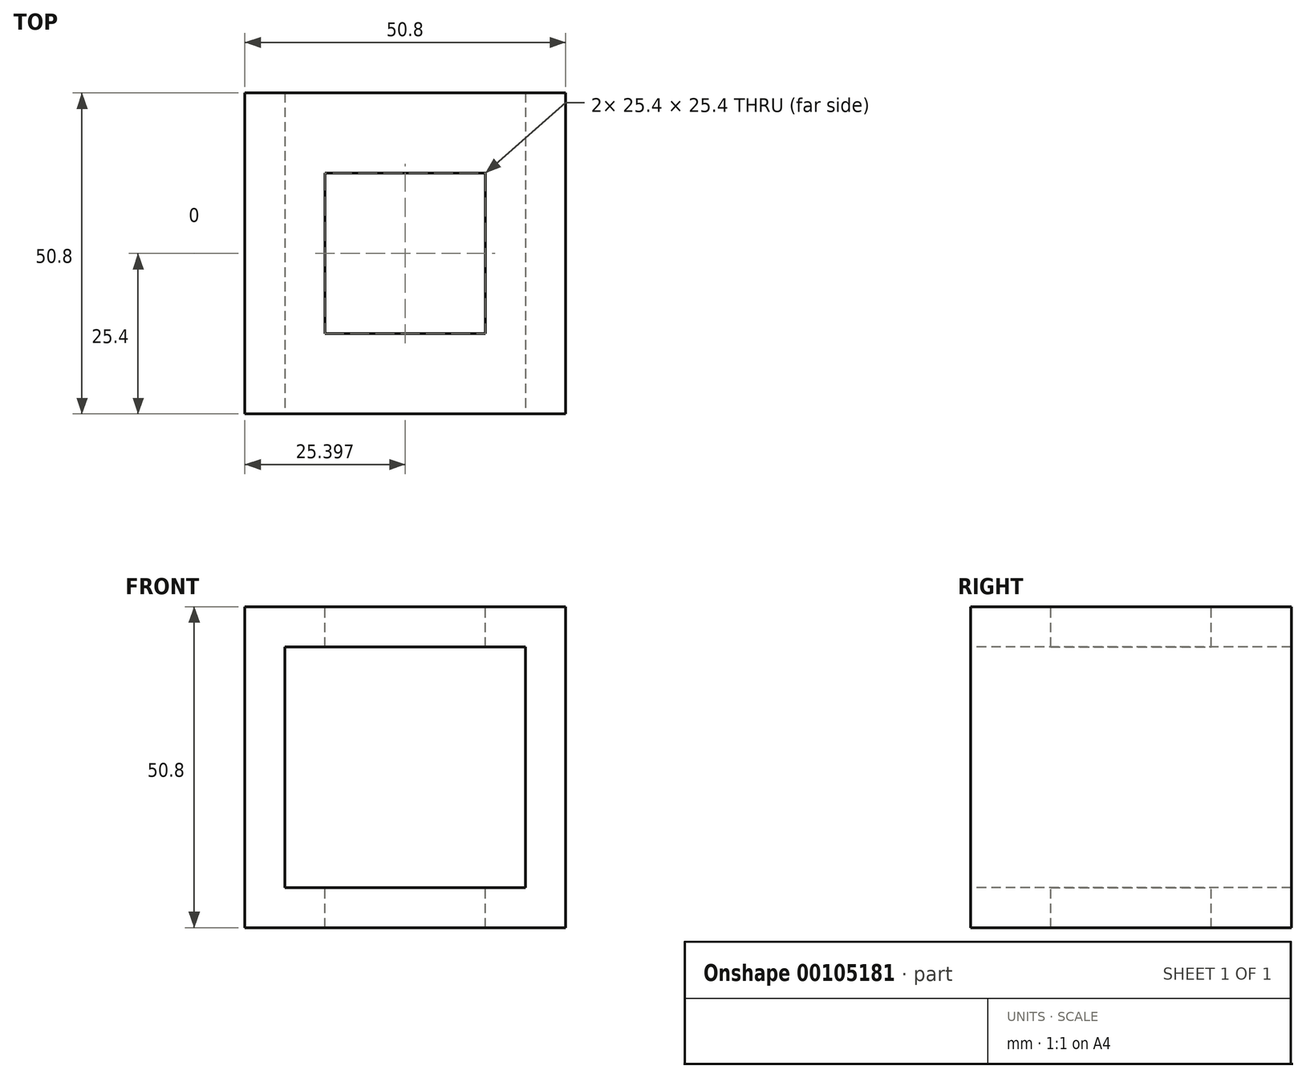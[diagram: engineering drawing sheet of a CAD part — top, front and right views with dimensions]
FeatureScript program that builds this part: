
annotation { "Feature Type Name" : "Feature", "Feature Type Description" : "" }
export const myFeature = defineFeature(function(context is Context, id is Id, definition is map)
    precondition{}
    {
        {
            var Q0;
            Q0=qCreatedBy(makeId("Front.planeOp"),FACE);
            var sketch = newSketch(context, id + "F0", { "sketchPlane" : qUnion([Q0])});
            skLineSegment(sketch, "E0", {"start": v(-98.96, 44.89) * mm, "end": v(-98.96, -5.91) * mm});
            skLineSegment(sketch, "E1", {"start": v(-98.96, -5.91) * mm, "end": v(-48.16, -5.91) * mm});
            skLineSegment(sketch, "E2", {"start": v(-48.16, -5.91) * mm, "end": v(-48.16, 44.89) * mm});
            skLineSegment(sketch, "E3", {"start": v(-48.16, 44.89) * mm, "end": v(-98.96, 44.89) * mm});
            skSolve(sketch);
        }
        {
            var Q0;
            Q0 = qSketchRegion(id + "F0", true);
            extrude(context, id + "F1", {"entities" : qUnion([Q0]), "depth" : 50.8 * mm});
        }
        {
            var Q0;
            Q0=makeQuery(id+"F1.opExtrude","CAP_FACE",FACE,{"disambiguationData":[OSD([sQuery(id+"F0.wireOp",EDGE,"E0"),sQuery(id+"F0.wireOp",EDGE,"E1"),sQuery(id+"F0.wireOp",EDGE,"E2"),sQuery(id+"F0.wireOp",EDGE,"E3")])],"isStart":false});
            var sketch = newSketch(context, id + "F2", { "sketchPlane" : qUnion([Q0])});
            skLineSegment(sketch, "E4.bottom", {"start": v(-92.61, 38.54) * mm, "end": v(-54.51, 38.54) * mm});
            skLineSegment(sketch, "E4.top", {"start": v(-92.61, 0.44) * mm, "end": v(-54.51, 0.44) * mm});
            skLineSegment(sketch, "E4.left", {"start": v(-92.61, 38.54) * mm, "end": v(-92.61, 0.44) * mm});
            skLineSegment(sketch, "E4.right", {"start": v(-54.51, 38.54) * mm, "end": v(-54.51, 0.44) * mm});
            skLineSegment(sketch, "E5", {"start": v(-98.96, 44.89) * mm, "end": v(-48.16, -5.91) * mm, "construction": true});
            skSolve(sketch);
        }
        {
            var Q0;
            Q0=makeQuery(id+"F2.imprint","IMPRINT",FACE,{"disambiguationData":[TD([[makeQuery(id+"F2.imprint","IMPRINT",EDGE,{"derivedFrom":sQuery(id+"F2.wireOp",EDGE,"E4.bottom")}),-1.0]])]});
            extrude(context, id + "F3", {"entities" : qUnion([Q0]), "operationType" : NewBodyOperationType.REMOVE, "endBound" : BoundingType.THROUGH_ALL, "oppositeDirection" : true, "depth" : 25.4 * mm});
        }
        {
            var Q0;
            Q0=makeQuery(id+"F1.opExtrude","SWEPT_FACE",FACE,{"disambiguationData":[OSD([sQuery(id+"F0.wireOp",EDGE,"E3")])]});
            var sketch = newSketch(context, id + "F4", { "sketchPlane" : qUnion([Q0])});
            skLineSegment(sketch, "E6.bottom", {"start": v(-86.26, -12.7) * mm, "end": v(-60.86, -12.7) * mm});
            skLineSegment(sketch, "E6.top", {"start": v(-86.26, -38.1) * mm, "end": v(-60.86, -38.1) * mm});
            skLineSegment(sketch, "E6.left", {"start": v(-86.26, -12.7) * mm, "end": v(-86.26, -38.1) * mm});
            skLineSegment(sketch, "E6.right", {"start": v(-60.86, -12.7) * mm, "end": v(-60.86, -38.1) * mm});
            skSolve(sketch);
        }
        {
            var Q0;
            Q0=makeQuery(id+"F4.imprint","IMPRINT",FACE,{"disambiguationData":[TD([[makeQuery(id+"F4.imprint","IMPRINT",EDGE,{"derivedFrom":sQuery(id+"F4.wireOp",EDGE,"E6.bottom")}),-1.0]])]});
            var Q1;
            Q1=sQuery(id+"F4.wireOp",EDGE,"E6.bottom");
            var Q2;
            Q2=sQuery(id+"F4.wireOp",EDGE,"E6.left");
            var Q3;
            Q3=sQuery(id+"F4.wireOp",EDGE,"E6.top");
            var Q4;
            Q4=sQuery(id+"F4.wireOp",EDGE,"E6.right");
            extrude(context, id + "F5", {"entities" : qUnion([Q0]), "operationType" : NewBodyOperationType.REMOVE, "surfaceEntities" : qUnion([Q1, Q2, Q3, Q4]), "endBound" : BoundingType.THROUGH_ALL, "oppositeDirection" : true, "depth" : 25.4 * mm});
        }
    });
